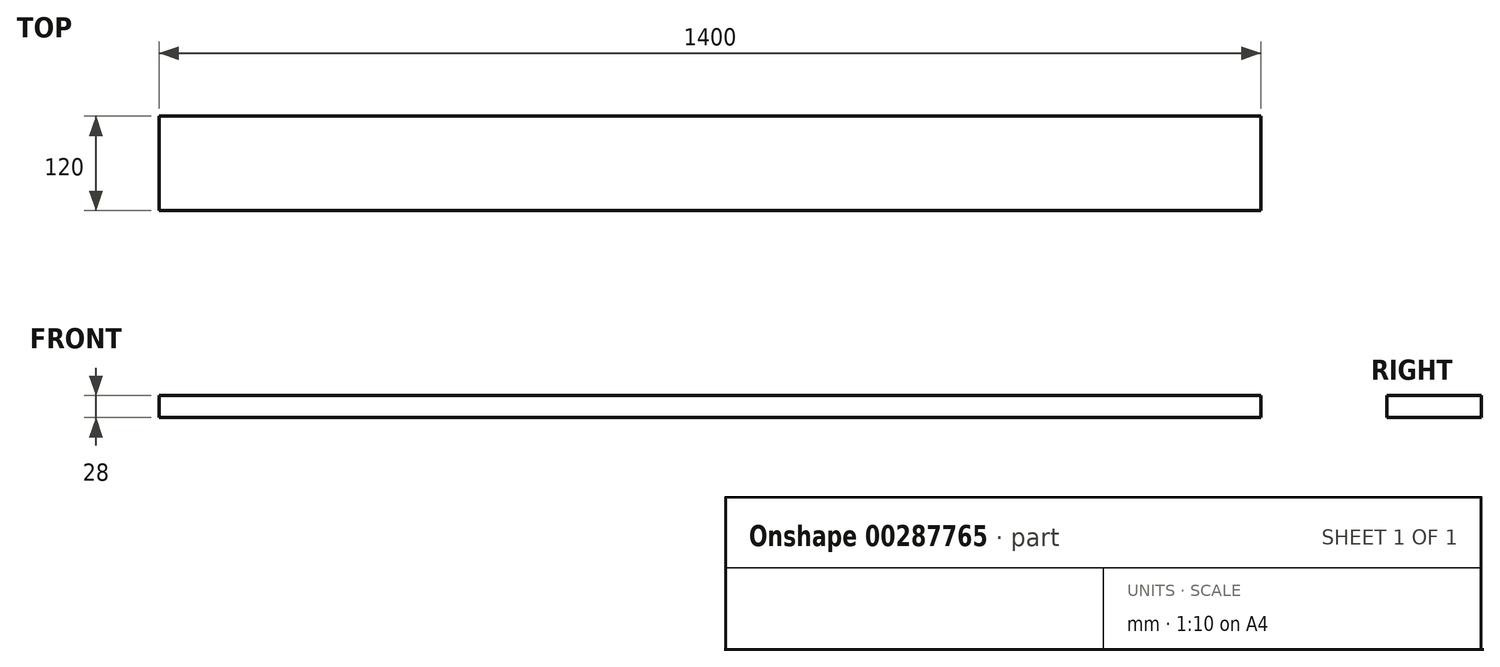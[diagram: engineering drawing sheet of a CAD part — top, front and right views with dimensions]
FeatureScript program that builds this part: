
annotation { "Feature Type Name" : "Feature", "Feature Type Description" : "" }
export const myFeature = defineFeature(function(context is Context, id is Id, definition is map)
    precondition{}
    {
        {
            var Q0;
            Q0=qCreatedBy(makeId("Right.planeOp"),FACE);
            var sketch = newSketch(context, id + "F0", { "sketchPlane" : qUnion([Q0])});
            skLineSegment(sketch, "E0.bottom", {"start": v(120, 28) * mm, "end": v(0, 28) * mm});
            skLineSegment(sketch, "E0.top", {"start": v(120, 0) * mm, "end": v(0, 0) * mm});
            skLineSegment(sketch, "E0.left", {"start": v(120, 28) * mm, "end": v(120, 0) * mm});
            skLineSegment(sketch, "E0.right", {"start": v(0, 28) * mm, "end": v(0, 0) * mm});
            skSolve(sketch);
        }
        {
            var Q0;
            Q0 = qSketchRegion(id + "F0", true);
            extrude(context, id + "F1", {"entities" : qUnion([Q0]), "depth" : 1400 * mm});
        }
    });
